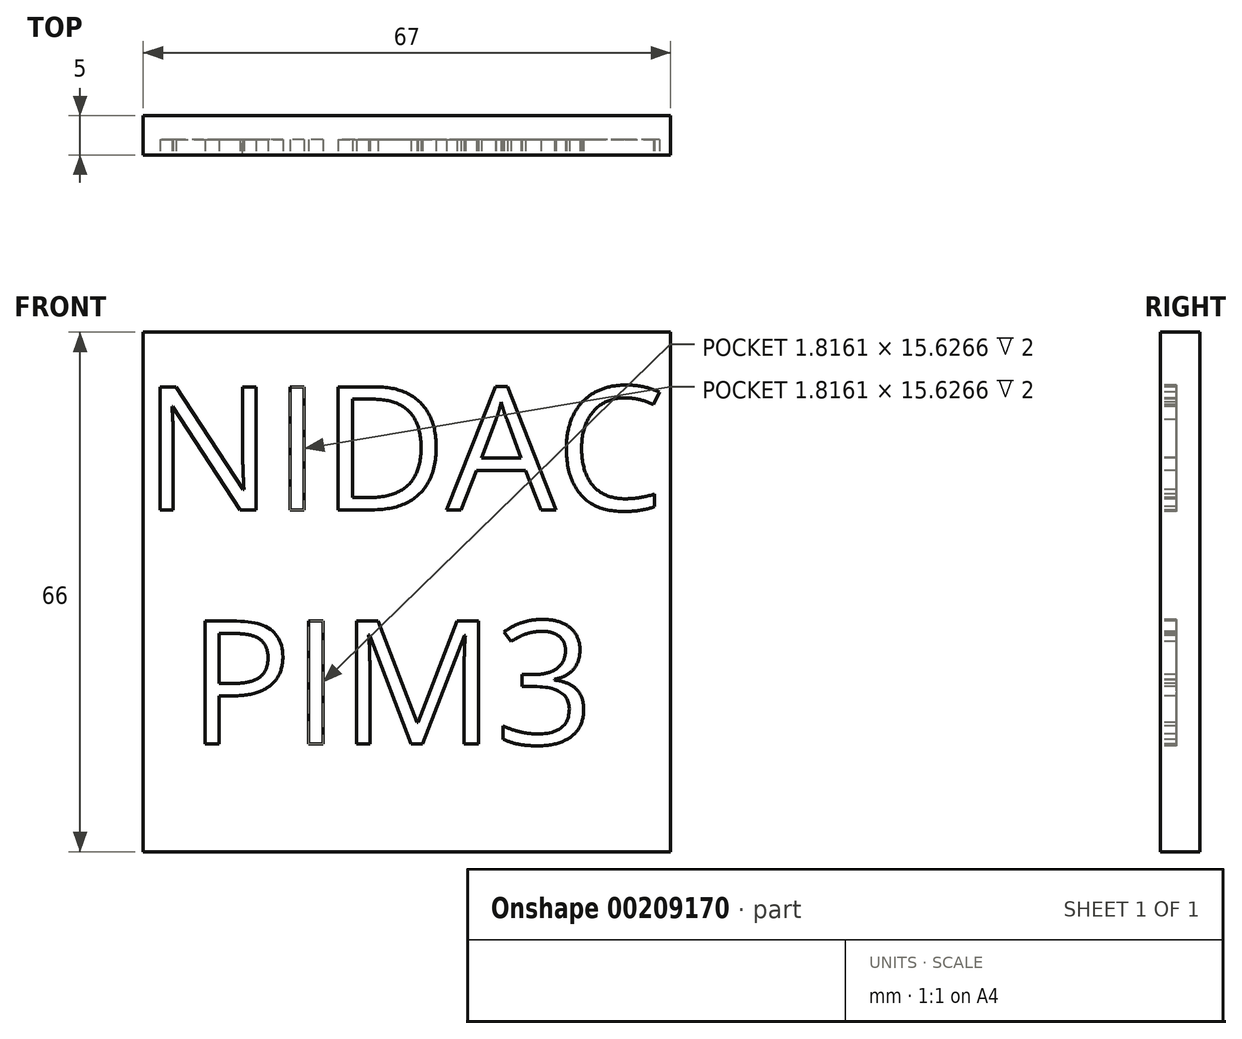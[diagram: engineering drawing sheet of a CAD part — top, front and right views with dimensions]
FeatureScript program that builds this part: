
annotation { "Feature Type Name" : "Feature", "Feature Type Description" : "" }
export const myFeature = defineFeature(function(context is Context, id is Id, definition is map)
    precondition{}
    {
        {
            var Q0;
            Q0=qCreatedBy(makeId("Front.planeOp"),FACE);
            var sketch = newSketch(context, id + "F0", { "sketchPlane" : qUnion([Q0])});
            skLineSegment(sketch, "E0.bottom", {"start": v(33.5, 33) * mm, "end": v(-33.5, 33) * mm});
            skLineSegment(sketch, "E0.top", {"start": v(33.5, -33) * mm, "end": v(-33.5, -33) * mm});
            skLineSegment(sketch, "E0.left", {"start": v(33.5, 33) * mm, "end": v(33.5, -33) * mm});
            skLineSegment(sketch, "E0.right", {"start": v(-33.5, 33) * mm, "end": v(-33.5, -33) * mm});
            skPoint(sketch, "E0.middle", {"position": v(0, 0) * mm});
            skSolve(sketch);
        }
        {
            var Q0;
            Q0 = qSketchRegion(id + "F0", true);
            extrude(context, id + "F1", {"entities" : qUnion([Q0]), "depth" : 5 * mm});
        }
        {
            var Q0;
            Q0=makeQuery(id+"F1.opExtrude","CAP_FACE",FACE,{"disambiguationData":[OSD([sQuery(id+"F0.wireOp",EDGE,"E0.bottom"),sQuery(id+"F0.wireOp",EDGE,"E0.top"),sQuery(id+"F0.wireOp",EDGE,"E0.left"),sQuery(id+"F0.wireOp",EDGE,"E0.right")])],"isStart":false});
            var sketch = newSketch(context, id + "F2", { "sketchPlane" : qUnion([Q0])});
            skText(sketch, "E1", { "text": "NIDAC\n PIM3", "fontName": "OpenSans-Regular.ttf"});
            const initialGuessF2  = {"E1": [-0.0335, 0.01044, 1, 0, 0.01576]};
            skSetInitialGuess(sketch, initialGuessF2);
            skSolve(sketch);
        }
        {
            var Q0;
            Q0 = qSketchRegion(id + "F2", true);
            extrude(context, id + "F3", {"entities" : qUnion([Q0]), "operationType" : NewBodyOperationType.REMOVE, "oppositeDirection" : true, "depth" : 2 * mm});
        }
    });
